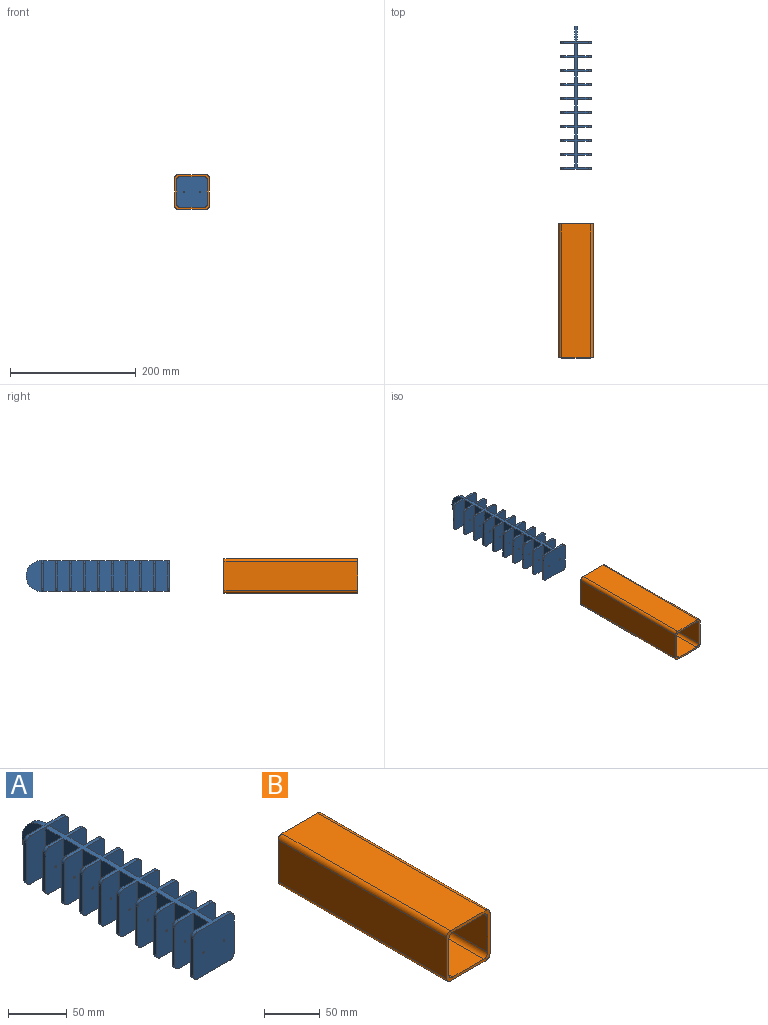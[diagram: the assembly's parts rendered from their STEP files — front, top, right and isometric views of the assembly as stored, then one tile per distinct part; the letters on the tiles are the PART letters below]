
ASSEMBLY  parts=2 mates=1
PART A: 141 faces, bbox 50x228.2x50 mm
  f0: plane 50x22.65mm, normal (0,1,0), area 1121.8mm2, adj f111,f112,f113,f118,f119,f120
  f1: plane 48.7x19mm, normal (1,0,0), area 925.3mm2, adj f19,f20,f72,f114
  f2: plane 48.7x19mm, normal (1,0,0), area 925.3mm2, adj f19,f20,f69,f71
  f3: plane 48.7x19mm, normal (1,0,0), area 925.3mm2, adj f19,f20,f66,f68
  f4: plane 48.7x19mm, normal (1,0,0), area 925.3mm2, adj f19,f20,f63,f65
  f5: plane 48.7x19mm, normal (1,0,0), area 925.3mm2, adj f19,f20,f60,f62
  f6: plane 48.7x19mm, normal (1,0,0), area 925.3mm2, adj f19,f20,f57,f59
  f7: plane 48.7x19mm, normal (1,0,0), area 925.3mm2, adj f19,f20,f54,f56
  f8: plane 48.7x19mm, normal (1,0,0), area 925.3mm2, adj f19,f20,f51,f53
  f9: plane 48.7x19mm, normal (1,0,0), area 925.3mm2, adj f19,f20,f48,f50
  f10: plane 48.7x19mm, normal (-1,0,0), area 925.3mm2, adj f19,f20,f44,f46
  f11: plane 48.7x19mm, normal (-1,0,0), area 925.3mm2, adj f19,f20,f41,f43
  f12: plane 48.7x19mm, normal (-1,0,0), area 925.3mm2, adj f19,f20,f38,f40
  f13: plane 48.7x19mm, normal (-1,0,0), area 925.3mm2, adj f19,f20,f35,f37
  f14: plane 48.7x19mm, normal (-1,0,0), area 925.3mm2, adj f19,f20,f32,f34
  f15: plane 48.7x19mm, normal (-1,0,0), area 925.3mm2, adj f19,f20,f29,f31
  f16: plane 48.7x19mm, normal (-1,0,0), area 925.3mm2, adj f19,f20,f26,f28
  f17: plane 48.7x19mm, normal (-1,0,0), area 925.3mm2, adj f19,f20,f23,f25
  f18: plane 48.7x19mm, normal (-1,0,0), area 925.3mm2, adj f19,f20,f22,f114
  f19: plane 200x38.7mm, normal (0,0,1), area 1926mm2, adj f1,f2,f3,f4,f5,f6,f7,f8
  f20: plane 200x38.7mm, normal (0,0,-1), area 1926mm2, adj f1,f2,f3,f4,f5,f6,f7,f8
  f21: plane 48.7x48.7mm, normal (0,-1,0), area 2343.9mm2, adj f19,f20,f47,f49,f90,f91,f92,f93
  f22: plane 48.7x22mm, normal (0,1,0), area 1057.5mm2, adj f18,f19,f20,f24,f108,f109,f140
  f23: plane 48.7x22mm, normal (0,-1,0), area 1057.5mm2, adj f17,f19,f20,f24,f108,f109,f140
  f24: plane 38.7x3.2mm, normal (-1,0,0), area 123.8mm2, adj f22,f23,f108,f109
  f25: plane 48.7x22mm, normal (0,1,0), area 1057.5mm2, adj f17,f19,f20,f27,f106,f107,f139
  f26: plane 48.7x22mm, normal (0,-1,0), area 1057.5mm2, adj f16,f19,f20,f27,f106,f107,f139
  f27: plane 38.7x3.2mm, normal (-1,0,0), area 123.8mm2, adj f25,f26,f106,f107
  f28: plane 48.7x22mm, normal (0,1,0), area 1057.5mm2, adj f16,f19,f20,f30,f104,f105,f138
  f29: plane 48.7x22mm, normal (0,-1,0), area 1057.5mm2, adj f15,f19,f20,f30,f104,f105,f138
  f30: plane 38.7x3.2mm, normal (-1,0,0), area 123.8mm2, adj f28,f29,f104,f105
  f31: plane 48.7x22mm, normal (0,1,0), area 1057.5mm2, adj f15,f19,f20,f33,f102,f103,f137
  f32: plane 48.7x22mm, normal (0,-1,0), area 1057.5mm2, adj f14,f19,f20,f33,f102,f103,f137
  f33: plane 38.7x3.2mm, normal (-1,0,0), area 123.8mm2, adj f31,f32,f102,f103
  f34: plane 48.7x22mm, normal (0,1,0), area 1057.5mm2, adj f14,f19,f20,f36,f100,f101,f136
  f35: plane 48.7x22mm, normal (0,-1,0), area 1057.5mm2, adj f13,f19,f20,f36,f100,f101,f136
  f36: plane 38.7x3.2mm, normal (-1,0,0), area 123.8mm2, adj f34,f35,f100,f101
  f37: plane 48.7x22mm, normal (0,1,0), area 1057.5mm2, adj f13,f19,f20,f39,f98,f99,f135
  f38: plane 48.7x22mm, normal (0,-1,0), area 1057.5mm2, adj f12,f19,f20,f39,f98,f99,f135
  f39: plane 38.7x3.2mm, normal (-1,0,0), area 123.8mm2, adj f37,f38,f98,f99
  f40: plane 48.7x22mm, normal (0,1,0), area 1057.5mm2, adj f12,f19,f20,f42,f96,f97,f134
  f41: plane 48.7x22mm, normal (0,-1,0), area 1057.5mm2, adj f11,f19,f20,f42,f96,f97,f134
  f42: plane 38.7x3.2mm, normal (-1,0,0), area 123.8mm2, adj f40,f41,f96,f97
  f43: plane 48.7x22mm, normal (0,1,0), area 1057.5mm2, adj f11,f19,f20,f45,f94,f95,f133
  f44: plane 48.7x22mm, normal (0,-1,0), area 1057.5mm2, adj f10,f19,f20,f45,f94,f95,f133
  f45: plane 38.7x3.2mm, normal (-1,0,0), area 123.8mm2, adj f43,f44,f94,f95
  f46: plane 48.7x22mm, normal (0,1,0), area 1057.5mm2, adj f10,f19,f20,f47,f92,f93,f132
  f47: plane 38.7x3.4mm, normal (-1,0,0), area 131.6mm2, adj f21,f46,f92,f93
  f48: plane 48.7x22mm, normal (0,1,0), area 1057.5mm2, adj f9,f19,f20,f49,f90,f91,f131
  f49: plane 38.7x3.4mm, normal (1,0,0), area 131.6mm2, adj f21,f48,f90,f91
  f50: plane 48.7x22mm, normal (0,-1,0), area 1057.5mm2, adj f9,f19,f20,f52,f88,f89,f130
  f51: plane 48.7x22mm, normal (0,1,0), area 1057.5mm2, adj f8,f19,f20,f52,f88,f89,f130
  f52: plane 38.7x3.2mm, normal (1,0,0), area 123.8mm2, adj f50,f51,f88,f89
  f53: plane 48.7x22mm, normal (0,-1,0), area 1057.5mm2, adj f8,f19,f20,f55,f86,f87,f129
  f54: plane 48.7x22mm, normal (0,1,0), area 1057.5mm2, adj f7,f19,f20,f55,f86,f87,f129
  f55: plane 38.7x3.2mm, normal (1,0,0), area 123.8mm2, adj f53,f54,f86,f87
  f56: plane 48.7x22mm, normal (0,-1,0), area 1057.5mm2, adj f7,f19,f20,f58,f84,f85,f128
  f57: plane 48.7x22mm, normal (0,1,0), area 1057.5mm2, adj f6,f19,f20,f58,f84,f85,f128
  f58: plane 38.7x3.2mm, normal (1,0,0), area 123.8mm2, adj f56,f57,f84,f85
  f59: plane 48.7x22mm, normal (0,-1,0), area 1057.5mm2, adj f6,f19,f20,f61,f82,f83,f127
  f60: plane 48.7x22mm, normal (0,1,0), area 1057.5mm2, adj f5,f19,f20,f61,f82,f83,f127
  f61: plane 38.7x3.2mm, normal (1,0,0), area 123.8mm2, adj f59,f60,f82,f83
  f62: plane 48.7x22mm, normal (0,-1,0), area 1057.5mm2, adj f5,f19,f20,f64,f80,f81,f126
  f63: plane 48.7x22mm, normal (0,1,0), area 1057.5mm2, adj f4,f19,f20,f64,f80,f81,f126
  f64: plane 38.7x3.2mm, normal (1,0,0), area 123.8mm2, adj f62,f63,f80,f81
  f65: plane 48.7x22mm, normal (0,-1,0), area 1057.5mm2, adj f4,f19,f20,f67,f78,f79,f125
  f66: plane 48.7x22mm, normal (0,1,0), area 1057.5mm2, adj f3,f19,f20,f67,f78,f79,f125
  f67: plane 38.7x3.2mm, normal (1,0,0), area 123.8mm2, adj f65,f66,f78,f79
  f68: plane 48.7x22mm, normal (0,-1,0), area 1057.5mm2, adj f3,f19,f20,f70,f76,f77,f124
  f69: plane 48.7x22mm, normal (0,1,0), area 1057.5mm2, adj f2,f19,f20,f70,f76,f77,f124
  f70: plane 38.7x3.2mm, normal (1,0,0), area 123.8mm2, adj f68,f69,f76,f77
  f71: plane 48.7x22mm, normal (0,-1,0), area 1057.5mm2, adj f2,f19,f20,f73,f74,f75,f123
  f72: plane 48.7x22mm, normal (0,1,0), area 1057.5mm2, adj f1,f19,f20,f73,f74,f75,f123
  f73: plane 38.7x3.2mm, normal (1,0,0), area 123.8mm2, adj f71,f72,f74,f75
  f74: cylinder r=5mm len=5mm, axis (0,-1,0), area 25.1mm2, adj f20,f71,f72,f73
  f75: cylinder r=5mm len=5mm, axis (0,1,0), area 25.1mm2, adj f19,f71,f72,f73
  f76: cylinder r=5mm len=5mm, axis (0,-1,0), area 25.1mm2, adj f20,f68,f69,f70
  f77: cylinder r=5mm len=5mm, axis (0,1,0), area 25.1mm2, adj f19,f68,f69,f70
  f78: cylinder r=5mm len=5mm, axis (0,-1,0), area 25.1mm2, adj f20,f65,f66,f67
  f79: cylinder r=5mm len=5mm, axis (0,1,0), area 25.1mm2, adj f19,f65,f66,f67
  f80: cylinder r=5mm len=5mm, axis (0,-1,0), area 25.1mm2, adj f20,f62,f63,f64
  f81: cylinder r=5mm len=5mm, axis (0,1,0), area 25.1mm2, adj f19,f62,f63,f64
  f82: cylinder r=5mm len=5mm, axis (0,-1,0), area 25.1mm2, adj f20,f59,f60,f61
  f83: cylinder r=5mm len=5mm, axis (0,1,0), area 25.1mm2, adj f19,f59,f60,f61
  f84: cylinder r=5mm len=5mm, axis (0,-1,0), area 25.1mm2, adj f20,f56,f57,f58
  f85: cylinder r=5mm len=5mm, axis (0,1,0), area 25.1mm2, adj f19,f56,f57,f58
  f86: cylinder r=5mm len=5mm, axis (0,-1,0), area 25.1mm2, adj f20,f53,f54,f55
  f87: cylinder r=5mm len=5mm, axis (0,1,0), area 25.1mm2, adj f19,f53,f54,f55
  f88: cylinder r=5mm len=5mm, axis (0,-1,0), area 25.1mm2, adj f20,f50,f51,f52
  f89: cylinder r=5mm len=5mm, axis (0,1,0), area 25.1mm2, adj f19,f50,f51,f52
  f90: cylinder r=5mm len=5mm, axis (0,1,0), area 26.7mm2, adj f19,f21,f48,f49
  f91: cylinder r=5mm len=5mm, axis (0,-1,0), area 26.7mm2, adj f20,f21,f48,f49
  f92: cylinder r=5mm len=5mm, axis (0,-1,0), area 26.7mm2, adj f20,f21,f46,f47
  f93: cylinder r=5mm len=5mm, axis (0,1,0), area 26.7mm2, adj f19,f21,f46,f47
  f94: cylinder r=5mm len=5mm, axis (0,-1,0), area 25.1mm2, adj f20,f43,f44,f45
  f95: cylinder r=5mm len=5mm, axis (0,1,0), area 25.1mm2, adj f19,f43,f44,f45
  f96: cylinder r=5mm len=5mm, axis (0,-1,0), area 25.1mm2, adj f20,f40,f41,f42
  f97: cylinder r=5mm len=5mm, axis (0,1,0), area 25.1mm2, adj f19,f40,f41,f42
  f98: cylinder r=5mm len=5mm, axis (0,-1,0), area 25.1mm2, adj f20,f37,f38,f39
  f99: cylinder r=5mm len=5mm, axis (0,1,0), area 25.1mm2, adj f19,f37,f38,f39
  f100: cylinder r=5mm len=5mm, axis (0,-1,0), area 25.1mm2, adj f20,f34,f35,f36
  f101: cylinder r=5mm len=5mm, axis (0,1,0), area 25.1mm2, adj f19,f34,f35,f36
  f102: cylinder r=5mm len=5mm, axis (0,-1,0), area 25.1mm2, adj f20,f31,f32,f33
  f103: cylinder r=5mm len=5mm, axis (0,1,0), area 25.1mm2, adj f19,f31,f32,f33
  f104: cylinder r=5mm len=5mm, axis (0,-1,0), area 25.1mm2, adj f20,f28,f29,f30
  f105: cylinder r=5mm len=5mm, axis (0,1,0), area 25.1mm2, adj f19,f28,f29,f30
  f106: cylinder r=5mm len=5mm, axis (0,-1,0), area 25.1mm2, adj f20,f25,f26,f27
  f107: cylinder r=5mm len=5mm, axis (0,1,0), area 25.1mm2, adj f19,f25,f26,f27
  f108: cylinder r=5mm len=5mm, axis (0,-1,0), area 25.1mm2, adj f20,f22,f23,f24
  f109: cylinder r=5mm len=5mm, axis (0,1,0), area 25.1mm2, adj f19,f22,f23,f24
  f110: plane 40x3.2mm, normal (-1,0,0), area 128mm2, adj f114,f115,f116,f117
  f111: plane 40x3.2mm, normal (0,0,-1), area 128mm2, adj f0,f114,f115,f116,f118,f122
  f112: plane 40x3.2mm, normal (1,0,0), area 128mm2, adj f0,f114,f118,f119
  f113: plane 40x3.2mm, normal (0,0,1), area 128mm2, adj f0,f114,f115,f117,f119,f122
  f114: plane 50x50mm, normal (0,-1,0), area 2249.6mm2, adj f1,f18,f19,f20,f110,f111,f112,f113
  f115: plane 50x22.65mm, normal (0,1,0), area 1121.8mm2, adj f110,f111,f113,f116,f117,f121
  f116: cylinder r=5mm len=5mm, axis (0,-1,0), area 25.1mm2, adj f110,f111,f114,f115
  f117: cylinder r=5mm len=5mm, axis (0,1,0), area 25.1mm2, adj f110,f113,f114,f115
  f118: cylinder r=5mm len=5mm, axis (0,1,0), area 25.1mm2, adj f0,f111,f112,f114
  f119: cylinder r=5mm len=5mm, axis (0,-1,0), area 25.1mm2, adj f0,f112,f113,f114
  f120: plane 50x25mm, normal (1,0,0), area 981.7mm2, adj f0,f122
  f121: plane 50x25mm, normal (-1,0,0), area 981.7mm2, adj f115,f122
  f122: cylinder r=25mm len=50mm, axis (1,0,0), area 369.1mm2, adj f111,f113,f120,f121
  f123: cylinder r=1mm len=3.2mm, axis (0,-1,0), area 20.1mm2, adj f71,f72
  f124: cylinder r=1mm len=3.2mm, axis (0,-1,0), area 20.1mm2, adj f68,f69
  f125: cylinder r=1mm len=3.2mm, axis (0,-1,0), area 20.1mm2, adj f65,f66
  f126: cylinder r=1mm len=3.2mm, axis (0,-1,0), area 20.1mm2, adj f62,f63
  f127: cylinder r=1mm len=3.2mm, axis (0,-1,0), area 20.1mm2, adj f59,f60
  f128: cylinder r=1mm len=3.2mm, axis (0,-1,0), area 20.1mm2, adj f56,f57
  f129: cylinder r=1mm len=3.2mm, axis (0,-1,0), area 20.1mm2, adj f53,f54
  f130: cylinder r=1mm len=3.2mm, axis (0,-1,0), area 20.1mm2, adj f50,f51
  f131: cylinder r=1mm len=3.4mm, axis (0,-1,0), area 21.4mm2, adj f21,f48
  f132: cylinder r=1mm len=3.4mm, axis (0,-1,0), area 21.4mm2, adj f21,f46
  f133: cylinder r=1mm len=3.2mm, axis (0,-1,0), area 20.1mm2, adj f43,f44
  f134: cylinder r=1mm len=3.2mm, axis (0,-1,0), area 20.1mm2, adj f40,f41
  f135: cylinder r=1mm len=3.2mm, axis (0,-1,0), area 20.1mm2, adj f37,f38
  f136: cylinder r=1mm len=3.2mm, axis (0,-1,0), area 20.1mm2, adj f34,f35
  f137: cylinder r=1mm len=3.2mm, axis (0,-1,0), area 20.1mm2, adj f31,f32
  f138: cylinder r=1mm len=3.2mm, axis (0,-1,0), area 20.1mm2, adj f28,f29
  f139: cylinder r=1mm len=3.2mm, axis (0,-1,0), area 20.1mm2, adj f25,f26
  f140: cylinder r=1mm len=3.2mm, axis (0,-1,0), area 20.1mm2, adj f22,f23
PART B: 27 faces, bbox 55x213.2x55 mm
  f0: plane 213.2x45mm, normal (0,0,-1), area 9594mm2, adj f4,f5,f15,f18
  f1: plane 213.2x45mm, normal (1,0,0), area 9594mm2, adj f4,f5,f15,f16
  f2: plane 213.2x45mm, normal (0,0,1), area 9594mm2, adj f4,f5,f16,f17
  f3: plane 213.2x45mm, normal (-1,0,0), area 9594mm2, adj f4,f5,f17,f18
  f4: plane 55x55mm, normal (0,-1,0), area 624mm2, adj f0,f1,f2,f3,f11,f12,f13,f14
  f5: plane 55x55mm, normal (0,1,0), area 424mm2, adj f0,f1,f2,f3,f6,f7,f8,f9
  f6: plane 41x3.2mm, normal (-1,0,0), area 131.2mm2, adj f5,f10,f23,f26
  f7: plane 41x3.2mm, normal (0,0,-1), area 131.2mm2, adj f5,f10,f23,f24
  f8: plane 41x3.2mm, normal (1,0,0), area 131.2mm2, adj f5,f10,f24,f25
  f9: plane 41x3.2mm, normal (0,0,1), area 131.2mm2, adj f5,f10,f25,f26
  f10: plane 51x51mm, normal (0,1,0), area 200mm2, adj f6,f7,f8,f9,f11,f12,f13,f14
  f11: plane 210x39mm, normal (0,0,-1), area 8190mm2, adj f4,f10,f19,f22
  f12: plane 210x39mm, normal (1,0,0), area 8190mm2, adj f4,f10,f19,f20
  f13: plane 210x39mm, normal (0,0,1), area 8190mm2, adj f4,f10,f20,f21
  f14: plane 210x39mm, normal (-1,0,0), area 8190mm2, adj f4,f10,f21,f22
  f15: cylinder r=5mm len=213.2mm, axis (0,-1,0), area 1674.5mm2, adj f0,f1,f4,f5
  f16: cylinder r=5mm len=213.2mm, axis (0,1,0), area 1674.5mm2, adj f1,f2,f4,f5
  f17: cylinder r=5mm len=213.2mm, axis (0,-1,0), area 1674.5mm2, adj f2,f3,f4,f5
  f18: cylinder r=5mm len=213.2mm, axis (0,1,0), area 1674.5mm2, adj f0,f3,f4,f5
  f19: cylinder r=5mm len=210mm, axis (0,1,0), area 1649.3mm2, adj f4,f10,f11,f12
  f20: cylinder r=5mm len=210mm, axis (0,-1,0), area 1649.3mm2, adj f4,f10,f12,f13
  f21: cylinder r=5mm len=210mm, axis (0,1,0), area 1649.3mm2, adj f4,f10,f13,f14
  f22: cylinder r=5mm len=210mm, axis (0,-1,0), area 1649.3mm2, adj f4,f10,f11,f14
  f23: cylinder r=5mm len=5mm, axis (0,1,0), area 25.1mm2, adj f5,f6,f7,f10
  f24: cylinder r=5mm len=5mm, axis (0,-1,0), area 25.1mm2, adj f5,f7,f8,f10
  f25: cylinder r=5mm len=5mm, axis (0,1,0), area 25.1mm2, adj f5,f8,f9,f10
  f26: cylinder r=5mm len=5mm, axis (0,-1,0), area 25.1mm2, adj f5,f6,f9,f10
PLACE A t=(-57.83,428.63,2.03)mm
PLACE B t=(-5.33,138.63,-0.47)mm fixed
MATE slider A.f21 <-> B.f4  axis (0,-1,0) through (-32.83,225.43,27.03)mm
